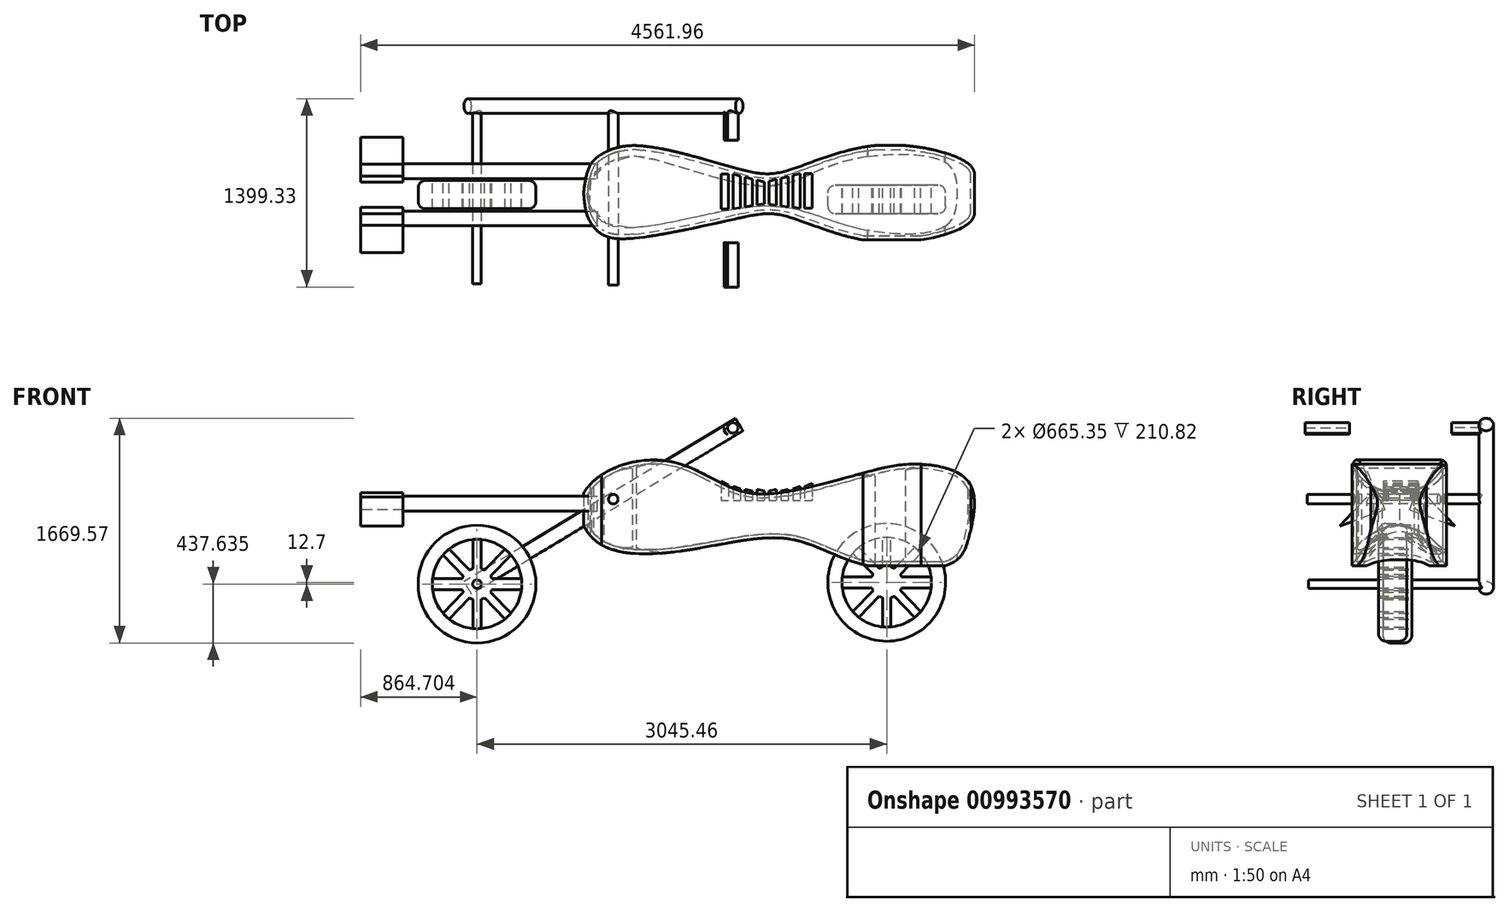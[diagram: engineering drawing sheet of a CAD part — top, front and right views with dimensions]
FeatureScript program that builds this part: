
annotation { "Feature Type Name" : "Feature", "Feature Type Description" : "" }
export const myFeature = defineFeature(function(context is Context, id is Id, definition is map)
    precondition{}
    {
        {
            var Q0;
            Q0=qCreatedBy(makeId("Front.planeOp"),FACE);
            var sketch = newSketch(context, id + "F0", { "sketchPlane" : qUnion([Q0])});
            skFitSpline(sketch, "E0", {"points": [v(-98.98, 13.69) * mm, v(-77.15, 35.34) * mm, v(-39.85, 38.35) * mm, v(-9.17, 24.51) * mm, v(18.5, 19.1) * mm, v(77.75, 32.33) * mm, v(110.84, 37.45) * mm, v(142.12, 25.72) * mm, v(142.12, -6.47) * mm, v(131.6, -23.61) * mm, v(76.55, -24.82) * mm, v(30.53, -8.87) * mm, v(-28.73, -15.19) * mm, v(-86.35, -12.18) * mm, v(-98.98, 13.69) * mm]});
            skSolve(sketch);
        }
        {
            var Q0;
            Q0=makeQuery(id+"F0.imprint","IMPRINT",FACE,{"disambiguationData":[TD([[makeQuery(id+"F0.imprint","IMPRINT",EDGE,{"derivedFrom":sQuery(id+"F0.wireOp",EDGE,"E0")}),-1.0]])]});
            extrude(context, id + "F1", {"entities" : qUnion([Q0]), "depth" : 58.42 * mm, "offsetDistance" : 25.4 * mm});
        }
        {
            var Q0;
            Q0=qCreatedBy(makeId("Top.planeOp"),FACE);
            var sketch = newSketch(context, id + "F2", { "sketchPlane" : qUnion([Q0])});
            skLineSegment(sketch, "E1", {"start": v(-96.89, 0) * mm, "end": v(144, 0) * mm});
            skFitSpline(sketch, "E2", {"points": [v(-96.89, -29.08) * mm, v(-92.88, -12.27) * mm, v(-85.74, -5.4) * mm, v(-64.33, 0) * mm, v(0, -14.66) * mm, v(26.78, -16.16) * mm, v(83.58, 0) * mm, v(143.04, -12.58) * mm, v(145.6, -29.08) * mm], "startDerivative": vector(25.51, 217.38) * mm, "endDerivative": vector(-17.37, -255.32) * mm});
            skFitSpline(sketch, "E3.MirrorCS", {"points": [v(-96.89, -29.08) * mm, v(-93.67, -45.57) * mm, v(-85.74, -54.8) * mm, v(-65.35, -57.37) * mm, v(0, -44.8) * mm, v(26.78, -43.3) * mm, v(83.58, -59.47) * mm, v(143.04, -46.89) * mm, v(145.6, -29.74) * mm], "startDerivative": vector(23.13, -272.3) * mm, "endDerivative": vector(-17.37, 255.32) * mm});
            skFitSpline(sketch, "E4", {"points": [v(-96.89, -29.08) * mm, v(-92.88, -12.27) * mm, v(-85.74, -5.4) * mm, v(-64.33, 0) * mm, v(0, -14.66) * mm, v(26.78, -16.16) * mm, v(83.58, 0) * mm, v(143.04, -12.58) * mm, v(145.6, -29.08) * mm, v(143.04, -46.89) * mm, v(83.58, -59.47) * mm, v(26.78, -43.3) * mm, v(0, -44.8) * mm, v(-65.35, -57.37) * mm, v(-85.74, -54.8) * mm, v(-93.67, -45.57) * mm, v(-96.89, -29.08) * mm]});
            skSolve(sketch);
        }
        {
            var Q0;
            {var subQ4=sQuery(id+"F2.wireOp",EDGE,"E3.MirrorCS");Q0=makeQuery(id+"F2.imprint","IMPRINT",FACE,{"disambiguationData":[TD([[makeQuery(id+"F2.imprint","IMPRINT",EDGE,{"derivedFrom":subQ4}),1.0]])]});}
            extrude(context, id + "F3", {"entities" : qUnion([Q0]), "operationType" : NewBodyOperationType.INTERSECT, "depth" : 68.58 * mm, "offsetDistance" : 25.4 * mm, "hasSecondDirection" : true, "secondDirectionOppositeDirection" : true, "secondDirectionDepth" : 25.4 * mm});
        }
        {
            var Q0;
            {var subQ0=sQuery(id+"F0.wireOp",EDGE,"E0");var subQ1=sQuery(id+"F2.wireOp",EDGE,"E4");var subQ2=sQuery(id+"F2.wireOp",EDGE,"E3.MirrorCS");var subQ3=makeQuery(id+"F2.imprint","INTERSECT",VERTEX,{"disambiguationData":[OD(8.0)],"derivedFrom":[subQ2,subQ1]});Q0=makeQuery(id+"F3.boolean.opBoolean","SPLIT",EDGE,{"disambiguationData":[TD([makeQuery(id+"F3.boolean.toolComplement.opBoolean","COPY",FACE,{"derivedFrom":makeQuery(id+"F3.opExtrude","SWEPT_FACE",FACE,{"disambiguationData":[OSD([subQ2]),TDD([makeQuery(id+"F2.imprint","IMPRINT",EDGE,{"disambiguationData":[TD([[subQ3,-1.0]])],"derivedFrom":subQ2})])]})})])],"derivedFrom":makeQuery(id+"F1.opExtrude","CAP_EDGE",EDGE,{"disambiguationData":[OSD([subQ0])],"isStart":false})});}
            var Q1;
            {var subQ0=sQuery(id+"F2.wireOp",EDGE,"E4");var subQ1=sQuery(id+"F2.wireOp",EDGE,"E3.MirrorCS");Q1=makeQuery(id+"F3.boolean.opBoolean","INTERSECT",EDGE,{"disambiguationData":[OD(1.0)],"derivedFrom":[makeQuery(id+"F1.opExtrude","SWEPT_FACE",FACE,{"disambiguationData":[OSD([sQuery(id+"F0.wireOp",EDGE,"E0")])]}),makeQuery(id+"F3.boolean.toolComplement.opBoolean","COPY",FACE,{"derivedFrom":makeQuery(id+"F3.opExtrude","SWEPT_FACE",FACE,{"disambiguationData":[OSD([subQ1]),TDD([makeQuery(id+"F2.imprint","IMPRINT",EDGE,{"disambiguationData":[TD([[makeQuery(id+"F2.imprint","INTERSECT",VERTEX,{"disambiguationData":[OD(8.0)],"derivedFrom":[subQ1,subQ0]}),-1.0]])],"derivedFrom":subQ1})])]})})]});}
            var Q2;
            {var subQ0=sQuery(id+"F2.wireOp",EDGE,"E4");var subQ1=sQuery(id+"F2.wireOp",EDGE,"E3.MirrorCS");Q2=makeQuery(id+"F3.boolean.opBoolean","INTERSECT",EDGE,{"disambiguationData":[OD(0.0)],"derivedFrom":[makeQuery(id+"F1.opExtrude","SWEPT_FACE",FACE,{"disambiguationData":[OSD([sQuery(id+"F0.wireOp",EDGE,"E0")])]}),makeQuery(id+"F3.boolean.toolComplement.opBoolean","COPY",FACE,{"derivedFrom":makeQuery(id+"F3.opExtrude","SWEPT_FACE",FACE,{"disambiguationData":[OSD([subQ1]),TDD([makeQuery(id+"F2.imprint","IMPRINT",EDGE,{"disambiguationData":[TD([[makeQuery(id+"F2.imprint","INTERSECT",VERTEX,{"disambiguationData":[OD(8.0)],"derivedFrom":[subQ1,subQ0]}),-1.0]])],"derivedFrom":subQ1})])]})})]});}
            var Q3;
            {var subQ0=sQuery(id+"F2.wireOp",EDGE,"E4");var subQ1=sQuery(id+"F2.wireOp",EDGE,"E3.MirrorCS");Q3=makeQuery(id+"F3.boolean.opBoolean","COPY",EDGE,{"derivedFrom":makeQuery(id+"F3.boolean.toolComplement.opBoolean","COPY",EDGE,{"derivedFrom":makeQuery(id+"F3.opExtrude","SWEPT_EDGE",EDGE,{"disambiguationData":[OSD([subQ1,subQ0]),TDD([makeQuery(id+"F2.imprint","INTERSECT",VERTEX,{"disambiguationData":[OD(9.0)],"derivedFrom":[subQ1,subQ0]})])]})})});}
            var Q4;
            Q4=makeQuery(id+"F3.boolean.opBoolean","INTERSECT",EDGE,{"derivedFrom":[makeQuery(id+"F1.opExtrude","CAP_FACE",FACE,{"disambiguationData":[OSD([sQuery(id+"F0.wireOp",EDGE,"E0")])],"isStart":false}),makeQuery(id+"F3.boolean.toolComplement.opBoolean","COPY",FACE,{"derivedFrom":makeQuery(id+"F3.opExtrude","CAP_FACE",FACE,{"disambiguationData":[OSD([sQuery(id+"F2.wireOp",EDGE,"E1"),sQuery(id+"F2.wireOp",EDGE,"E2"),sQuery(id+"F2.wireOp",EDGE,"E3.MirrorCS"),sQuery(id+"F2.wireOp",EDGE,"E4")])],"isStart":true})})]});
            var Q5;
            {var subQ0=sQuery(id+"F2.wireOp",EDGE,"E4");var subQ1=sQuery(id+"F2.wireOp",EDGE,"E3.MirrorCS");Q5=makeQuery(id+"F3.boolean.opBoolean","COPY",EDGE,{"derivedFrom":makeQuery(id+"F3.boolean.toolComplement.opBoolean","COPY",EDGE,{"derivedFrom":makeQuery(id+"F3.opExtrude","CAP_EDGE",EDGE,{"disambiguationData":[OSD([subQ1]),TDD([makeQuery(id+"F2.imprint","IMPRINT",EDGE,{"disambiguationData":[TD([[makeQuery(id+"F2.imprint","INTERSECT",VERTEX,{"disambiguationData":[OD(8.0)],"derivedFrom":[subQ1,subQ0]}),-1.0]])],"derivedFrom":subQ1})])],"isStart":true})})});}
            var Q6;
            {var subQ0=sQuery(id+"F2.wireOp",EDGE,"E4");var subQ1=sQuery(id+"F2.wireOp",EDGE,"E3.MirrorCS");Q6=makeQuery(id+"F3.boolean.opBoolean","INTERSECT",EDGE,{"disambiguationData":[OD(0.0)],"derivedFrom":[makeQuery(id+"F1.opExtrude","SWEPT_FACE",FACE,{"disambiguationData":[OSD([sQuery(id+"F0.wireOp",EDGE,"E0")])]}),makeQuery(id+"F3.boolean.toolComplement.opBoolean","COPY",FACE,{"derivedFrom":makeQuery(id+"F3.opExtrude","SWEPT_FACE",FACE,{"disambiguationData":[OSD([subQ0]),TDD([makeQuery(id+"F2.imprint","IMPRINT",EDGE,{"disambiguationData":[TD([[makeQuery(id+"F2.imprint","INTERSECT",VERTEX,{"disambiguationData":[OD(7.0)],"derivedFrom":[subQ1,subQ0]}),1.0]])],"derivedFrom":subQ0})])]})})]});}
            var Q7;
            {var subQ0=sQuery(id+"F2.wireOp",EDGE,"E4");var subQ1=sQuery(id+"F2.wireOp",EDGE,"E3.MirrorCS");Q7=makeQuery(id+"F3.boolean.opBoolean","INTERSECT",EDGE,{"disambiguationData":[OD(0.0)],"derivedFrom":[makeQuery(id+"F1.opExtrude","SWEPT_FACE",FACE,{"disambiguationData":[OSD([sQuery(id+"F0.wireOp",EDGE,"E0")])]}),makeQuery(id+"F3.boolean.toolComplement.opBoolean","COPY",FACE,{"derivedFrom":makeQuery(id+"F3.opExtrude","SWEPT_FACE",FACE,{"disambiguationData":[OSD([subQ1]),TDD([makeQuery(id+"F2.imprint","IMPRINT",EDGE,{"disambiguationData":[TD([[makeQuery(id+"F2.imprint","INTERSECT",VERTEX,{"disambiguationData":[OD(1.0)],"derivedFrom":[subQ1,subQ0]}),-1.0]])],"derivedFrom":subQ1})])]})})]});}
            var Q8;
            {var subQ0=sQuery(id+"F2.wireOp",EDGE,"E4");var subQ1=sQuery(id+"F2.wireOp",EDGE,"E3.MirrorCS");Q8=makeQuery(id+"F3.boolean.opBoolean","INTERSECT",EDGE,{"disambiguationData":[OD(0.0)],"derivedFrom":[makeQuery(id+"F1.opExtrude","SWEPT_FACE",FACE,{"disambiguationData":[OSD([sQuery(id+"F0.wireOp",EDGE,"E0")])]}),makeQuery(id+"F3.boolean.toolComplement.opBoolean","COPY",FACE,{"derivedFrom":makeQuery(id+"F3.opExtrude","SWEPT_FACE",FACE,{"disambiguationData":[OSD([subQ1]),TDD([makeQuery(id+"F2.imprint","IMPRINT",EDGE,{"disambiguationData":[TD([[makeQuery(id+"F2.imprint","INTERSECT",VERTEX,{"disambiguationData":[OD(0.0)],"derivedFrom":[subQ1,subQ0]}),1.0]])],"derivedFrom":subQ1})])]})})]});}
            var Q9;
            {var subQ0=sQuery(id+"F2.wireOp",EDGE,"E4");var subQ1=sQuery(id+"F2.wireOp",EDGE,"E3.MirrorCS");Q9=makeQuery(id+"F3.boolean.opBoolean","INTERSECT",EDGE,{"disambiguationData":[OD(0.0)],"derivedFrom":[makeQuery(id+"F1.opExtrude","SWEPT_FACE",FACE,{"disambiguationData":[OSD([sQuery(id+"F0.wireOp",EDGE,"E0")])]}),makeQuery(id+"F3.boolean.toolComplement.opBoolean","COPY",FACE,{"derivedFrom":makeQuery(id+"F3.opExtrude","SWEPT_FACE",FACE,{"disambiguationData":[OSD([subQ0]),TDD([makeQuery(id+"F2.imprint","IMPRINT",EDGE,{"disambiguationData":[TD([[makeQuery(id+"F2.imprint","INTERSECT",VERTEX,{"disambiguationData":[OD(5.0)],"derivedFrom":[subQ1,subQ0]}),1.0]])],"derivedFrom":subQ0})])]})})]});}
            var Q10;
            {var subQ0=sQuery(id+"F2.wireOp",EDGE,"E4");var subQ1=sQuery(id+"F2.wireOp",EDGE,"E3.MirrorCS");Q10=makeQuery(id+"F3.boolean.opBoolean","COPY",EDGE,{"derivedFrom":makeQuery(id+"F3.boolean.toolComplement.opBoolean","COPY",EDGE,{"derivedFrom":makeQuery(id+"F3.opExtrude","SWEPT_EDGE",EDGE,{"disambiguationData":[OSD([subQ1,subQ0]),TDD([makeQuery(id+"F2.imprint","INTERSECT",VERTEX,{"disambiguationData":[OD(4.0)],"derivedFrom":[subQ1,subQ0]})])]})})});}
            var Q11;
            {var subQ0=sQuery(id+"F2.wireOp",EDGE,"E4");var subQ1=sQuery(id+"F2.wireOp",EDGE,"E3.MirrorCS");Q11=makeQuery(id+"F3.boolean.opBoolean","INTERSECT",EDGE,{"disambiguationData":[OD(0.0)],"derivedFrom":[makeQuery(id+"F1.opExtrude","SWEPT_FACE",FACE,{"disambiguationData":[OSD([sQuery(id+"F0.wireOp",EDGE,"E0")])]}),makeQuery(id+"F3.boolean.toolComplement.opBoolean","COPY",FACE,{"derivedFrom":makeQuery(id+"F3.opExtrude","SWEPT_FACE",FACE,{"disambiguationData":[OSD([subQ1]),TDD([makeQuery(id+"F2.imprint","IMPRINT",EDGE,{"disambiguationData":[TD([[makeQuery(id+"F2.imprint","INTERSECT",VERTEX,{"disambiguationData":[OD(4.0)],"derivedFrom":[subQ1,subQ0]}),-1.0]])],"derivedFrom":subQ1})])]})})]});}
            var Q12;
            {var subQ0=sQuery(id+"F2.wireOp",EDGE,"E4");var subQ1=sQuery(id+"F2.wireOp",EDGE,"E3.MirrorCS");Q12=makeQuery(id+"F3.boolean.opBoolean","INTERSECT",EDGE,{"disambiguationData":[OD(1.0)],"derivedFrom":[makeQuery(id+"F1.opExtrude","SWEPT_FACE",FACE,{"disambiguationData":[OSD([sQuery(id+"F0.wireOp",EDGE,"E0")])]}),makeQuery(id+"F3.boolean.toolComplement.opBoolean","COPY",FACE,{"derivedFrom":makeQuery(id+"F3.opExtrude","SWEPT_FACE",FACE,{"disambiguationData":[OSD([subQ0]),TDD([makeQuery(id+"F2.imprint","IMPRINT",EDGE,{"disambiguationData":[TD([[makeQuery(id+"F2.imprint","INTERSECT",VERTEX,{"disambiguationData":[OD(5.0)],"derivedFrom":[subQ1,subQ0]}),1.0]])],"derivedFrom":subQ0})])]})})]});}
            var Q13;
            {var subQ0=sQuery(id+"F2.wireOp",EDGE,"E4");var subQ1=sQuery(id+"F2.wireOp",EDGE,"E3.MirrorCS");Q13=makeQuery(id+"F3.boolean.opBoolean","INTERSECT",EDGE,{"disambiguationData":[OD(1.0)],"derivedFrom":[makeQuery(id+"F1.opExtrude","SWEPT_FACE",FACE,{"disambiguationData":[OSD([sQuery(id+"F0.wireOp",EDGE,"E0")])]}),makeQuery(id+"F3.boolean.toolComplement.opBoolean","COPY",FACE,{"derivedFrom":makeQuery(id+"F3.opExtrude","SWEPT_FACE",FACE,{"disambiguationData":[OSD([subQ1]),TDD([makeQuery(id+"F2.imprint","IMPRINT",EDGE,{"disambiguationData":[TD([[makeQuery(id+"F2.imprint","INTERSECT",VERTEX,{"disambiguationData":[OD(4.0)],"derivedFrom":[subQ1,subQ0]}),-1.0]])],"derivedFrom":subQ1})])]})})]});}
            var Q14;
            {var subQ0=sQuery(id+"F2.wireOp",EDGE,"E4");var subQ1=sQuery(id+"F2.wireOp",EDGE,"E3.MirrorCS");Q14=makeQuery(id+"F3.boolean.opBoolean","INTERSECT",EDGE,{"disambiguationData":[OD(1.0)],"derivedFrom":[makeQuery(id+"F1.opExtrude","SWEPT_FACE",FACE,{"disambiguationData":[OSD([sQuery(id+"F0.wireOp",EDGE,"E0")])]}),makeQuery(id+"F3.boolean.toolComplement.opBoolean","COPY",FACE,{"derivedFrom":makeQuery(id+"F3.opExtrude","SWEPT_FACE",FACE,{"disambiguationData":[OSD([subQ1]),TDD([makeQuery(id+"F2.imprint","IMPRINT",EDGE,{"disambiguationData":[TD([[makeQuery(id+"F2.imprint","INTERSECT",VERTEX,{"disambiguationData":[OD(0.0)],"derivedFrom":[subQ1,subQ0]}),1.0]])],"derivedFrom":subQ1})])]})})]});}
            var Q15;
            {var subQ0=sQuery(id+"F2.wireOp",EDGE,"E4");var subQ1=sQuery(id+"F2.wireOp",EDGE,"E3.MirrorCS");Q15=makeQuery(id+"F3.boolean.opBoolean","INTERSECT",EDGE,{"disambiguationData":[OD(1.0)],"derivedFrom":[makeQuery(id+"F1.opExtrude","SWEPT_FACE",FACE,{"disambiguationData":[OSD([sQuery(id+"F0.wireOp",EDGE,"E0")])]}),makeQuery(id+"F3.boolean.toolComplement.opBoolean","COPY",FACE,{"derivedFrom":makeQuery(id+"F3.opExtrude","SWEPT_FACE",FACE,{"disambiguationData":[OSD([subQ1]),TDD([makeQuery(id+"F2.imprint","IMPRINT",EDGE,{"disambiguationData":[TD([[makeQuery(id+"F2.imprint","INTERSECT",VERTEX,{"disambiguationData":[OD(1.0)],"derivedFrom":[subQ1,subQ0]}),-1.0]])],"derivedFrom":subQ1})])]})})]});}
            var Q16;
            {var subQ0=sQuery(id+"F2.wireOp",EDGE,"E4");var subQ1=sQuery(id+"F2.wireOp",EDGE,"E3.MirrorCS");Q16=makeQuery(id+"F3.boolean.opBoolean","INTERSECT",EDGE,{"disambiguationData":[OD(1.0)],"derivedFrom":[makeQuery(id+"F1.opExtrude","SWEPT_FACE",FACE,{"disambiguationData":[OSD([sQuery(id+"F0.wireOp",EDGE,"E0")])]}),makeQuery(id+"F3.boolean.toolComplement.opBoolean","COPY",FACE,{"derivedFrom":makeQuery(id+"F3.opExtrude","SWEPT_FACE",FACE,{"disambiguationData":[OSD([subQ0]),TDD([makeQuery(id+"F2.imprint","IMPRINT",EDGE,{"disambiguationData":[TD([[makeQuery(id+"F2.imprint","INTERSECT",VERTEX,{"disambiguationData":[OD(7.0)],"derivedFrom":[subQ1,subQ0]}),1.0]])],"derivedFrom":subQ0})])]})})]});}
            var Q17;
            {var subQ0=sQuery(id+"F2.wireOp",EDGE,"E4");var subQ1=sQuery(id+"F2.wireOp",EDGE,"E2");Q17=makeQuery(id+"F3.boolean.opBoolean","INTERSECT",EDGE,{"disambiguationData":[OD(1.0)],"derivedFrom":[makeQuery(id+"F1.opExtrude","SWEPT_FACE",FACE,{"disambiguationData":[OSD([sQuery(id+"F0.wireOp",EDGE,"E0")])]}),makeQuery(id+"F3.boolean.toolComplement.opBoolean","COPY",FACE,{"derivedFrom":makeQuery(id+"F3.opExtrude","SWEPT_FACE",FACE,{"disambiguationData":[OSD([subQ1]),TDD([makeQuery(id+"F2.imprint","IMPRINT",EDGE,{"disambiguationData":[TD([[makeQuery(id+"F2.imprint","INTERSECT",VERTEX,{"disambiguationData":[OD(5.0)],"derivedFrom":[subQ1,subQ0]}),1.0]])],"derivedFrom":subQ1})])]})})]});}
            var Q18;
            {var subQ0=sQuery(id+"F2.wireOp",EDGE,"E4");var subQ1=sQuery(id+"F2.wireOp",EDGE,"E2");Q18=makeQuery(id+"F3.boolean.opBoolean","INTERSECT",EDGE,{"disambiguationData":[OD(1.0)],"derivedFrom":[makeQuery(id+"F1.opExtrude","SWEPT_FACE",FACE,{"disambiguationData":[OSD([sQuery(id+"F0.wireOp",EDGE,"E0")])]}),makeQuery(id+"F3.boolean.toolComplement.opBoolean","COPY",FACE,{"derivedFrom":makeQuery(id+"F3.opExtrude","SWEPT_FACE",FACE,{"disambiguationData":[OSD([subQ0]),TDD([makeQuery(id+"F2.imprint","IMPRINT",EDGE,{"disambiguationData":[TD([[makeQuery(id+"F2.imprint","INTERSECT",VERTEX,{"disambiguationData":[OD(5.0)],"derivedFrom":[subQ1,subQ0]}),-1.0]])],"derivedFrom":subQ0})])]})})]});}
            var Q19;
            {var subQ0=sQuery(id+"F2.wireOp",EDGE,"E4");var subQ1=sQuery(id+"F2.wireOp",EDGE,"E2");Q19=makeQuery(id+"F3.boolean.opBoolean","INTERSECT",EDGE,{"disambiguationData":[OD(1.0)],"derivedFrom":[makeQuery(id+"F1.opExtrude","SWEPT_FACE",FACE,{"disambiguationData":[OSD([sQuery(id+"F0.wireOp",EDGE,"E0")])]}),makeQuery(id+"F3.boolean.toolComplement.opBoolean","COPY",FACE,{"derivedFrom":makeQuery(id+"F3.opExtrude","SWEPT_FACE",FACE,{"disambiguationData":[OSD([subQ1]),TDD([makeQuery(id+"F2.imprint","IMPRINT",EDGE,{"disambiguationData":[TD([[makeQuery(id+"F2.imprint","INTERSECT",VERTEX,{"disambiguationData":[OD(6.0)],"derivedFrom":[subQ1,subQ0]}),-1.0]])],"derivedFrom":subQ1})])]})})]});}
            var Q20;
            {var subQ0=sQuery(id+"F2.wireOp",EDGE,"E4");var subQ1=sQuery(id+"F2.wireOp",EDGE,"E2");Q20=makeQuery(id+"F3.boolean.opBoolean","INTERSECT",EDGE,{"disambiguationData":[OD(1.0)],"derivedFrom":[makeQuery(id+"F1.opExtrude","SWEPT_FACE",FACE,{"disambiguationData":[OSD([sQuery(id+"F0.wireOp",EDGE,"E0")])]}),makeQuery(id+"F3.boolean.toolComplement.opBoolean","COPY",FACE,{"derivedFrom":makeQuery(id+"F3.opExtrude","SWEPT_FACE",FACE,{"disambiguationData":[OSD([subQ0]),TDD([makeQuery(id+"F2.imprint","IMPRINT",EDGE,{"disambiguationData":[TD([[makeQuery(id+"F2.imprint","INTERSECT",VERTEX,{"disambiguationData":[OD(7.0)],"derivedFrom":[subQ1,subQ0]}),-1.0]])],"derivedFrom":subQ0})])]})})]});}
            var Q21;
            {var subQ0=sQuery(id+"F0.wireOp",EDGE,"E0");var subQ1=sQuery(id+"F2.wireOp",EDGE,"E4");var subQ2=sQuery(id+"F2.wireOp",EDGE,"E2");Q21=makeQuery(id+"F3.boolean.opBoolean","SPLIT",EDGE,{"disambiguationData":[TD([makeQuery(id+"F1.opExtrude","SWEPT_FACE",FACE,{"disambiguationData":[OSD([subQ0])]}),makeQuery(id+"F1.opExtrude","CAP_FACE",FACE,{"disambiguationData":[OSD([subQ0])],"isStart":true}),makeQuery(id+"F3.boolean.toolComplement.opBoolean","COPY",FACE,{"derivedFrom":makeQuery(id+"F3.opExtrude","SWEPT_FACE",FACE,{"disambiguationData":[OSD([subQ2]),TDD([makeQuery(id+"F2.imprint","IMPRINT",EDGE,{"disambiguationData":[TD([[makeQuery(id+"F2.imprint","INTERSECT",VERTEX,{"disambiguationData":[OD(4.0)],"derivedFrom":[subQ2,subQ1]}),1.0]])],"derivedFrom":subQ2})])]})}),makeQuery(id+"F3.boolean.toolComplement.opBoolean","COPY",FACE,{"derivedFrom":makeQuery(id+"F3.opExtrude","SWEPT_FACE",FACE,{"disambiguationData":[OSD([subQ1]),TDD([makeQuery(id+"F2.imprint","IMPRINT",EDGE,{"disambiguationData":[TD([[makeQuery(id+"F2.imprint","INTERSECT",VERTEX,{"disambiguationData":[OD(7.0)],"derivedFrom":[subQ2,subQ1]}),-1.0]])],"derivedFrom":subQ1})])]})})])],"derivedFrom":makeQuery(id+"F1.opExtrude","CAP_EDGE",EDGE,{"disambiguationData":[OSD([subQ0])],"isStart":true})});}
            var Q22;
            {var subQ0=sQuery(id+"F2.wireOp",EDGE,"E4");Q22=makeQuery(id+"F3.boolean.opBoolean","INTERSECT",EDGE,{"disambiguationData":[OD(1.0)],"derivedFrom":[makeQuery(id+"F1.opExtrude","SWEPT_FACE",FACE,{"disambiguationData":[OSD([sQuery(id+"F0.wireOp",EDGE,"E0")])]}),makeQuery(id+"F3.boolean.toolComplement.opBoolean","COPY",FACE,{"derivedFrom":makeQuery(id+"F3.opExtrude","SWEPT_FACE",FACE,{"disambiguationData":[OSD([subQ0]),TDD([makeQuery(id+"F2.imprint","IMPRINT",EDGE,{"disambiguationData":[TD([[makeQuery(id+"F2.imprint","INTERSECT",VERTEX,{"disambiguationData":[OD(3.0)],"derivedFrom":[sQuery(id+"F2.wireOp",EDGE,"E2"),subQ0]}),-1.0]])],"derivedFrom":subQ0})])]})})]});}
            var Q23;
            {var subQ0=sQuery(id+"F0.wireOp",EDGE,"E0");var subQ1=sQuery(id+"F2.wireOp",EDGE,"E4");var subQ2=sQuery(id+"F2.wireOp",EDGE,"E2");Q23=makeQuery(id+"F3.boolean.opBoolean","SPLIT",EDGE,{"disambiguationData":[TD([makeQuery(id+"F1.opExtrude","SWEPT_FACE",FACE,{"disambiguationData":[OSD([subQ0])]}),makeQuery(id+"F1.opExtrude","CAP_FACE",FACE,{"disambiguationData":[OSD([subQ0])],"isStart":true}),makeQuery(id+"F3.boolean.toolComplement.opBoolean","COPY",FACE,{"derivedFrom":makeQuery(id+"F3.opExtrude","SWEPT_FACE",FACE,{"disambiguationData":[OSD([subQ2]),TDD([makeQuery(id+"F2.imprint","IMPRINT",EDGE,{"disambiguationData":[TD([[makeQuery(id+"F2.imprint","INTERSECT",VERTEX,{"disambiguationData":[OD(5.0)],"derivedFrom":[subQ2,subQ1]}),1.0]])],"derivedFrom":subQ2})])]})}),makeQuery(id+"F3.boolean.toolComplement.opBoolean","COPY",FACE,{"derivedFrom":makeQuery(id+"F3.opExtrude","SWEPT_FACE",FACE,{"disambiguationData":[OSD([subQ1]),TDD([makeQuery(id+"F2.imprint","IMPRINT",EDGE,{"disambiguationData":[TD([[makeQuery(id+"F2.imprint","INTERSECT",VERTEX,{"disambiguationData":[OD(3.0)],"derivedFrom":[subQ2,subQ1]}),-1.0]])],"derivedFrom":subQ1})])]})})]),OD(1.0)],"derivedFrom":makeQuery(id+"F1.opExtrude","CAP_EDGE",EDGE,{"disambiguationData":[OSD([subQ0])],"isStart":true})});}
            var Q24;
            {var subQ0=sQuery(id+"F2.wireOp",EDGE,"E4");var subQ1=sQuery(id+"F2.wireOp",EDGE,"E2");Q24=makeQuery(id+"F3.boolean.opBoolean","INTERSECT",EDGE,{"disambiguationData":[OD(1.0)],"derivedFrom":[makeQuery(id+"F1.opExtrude","SWEPT_FACE",FACE,{"disambiguationData":[OSD([sQuery(id+"F0.wireOp",EDGE,"E0")])]}),makeQuery(id+"F3.boolean.toolComplement.opBoolean","COPY",FACE,{"derivedFrom":makeQuery(id+"F3.opExtrude","SWEPT_FACE",FACE,{"disambiguationData":[OSD([subQ1]),TDD([makeQuery(id+"F2.imprint","IMPRINT",EDGE,{"disambiguationData":[TD([[makeQuery(id+"F2.imprint","INTERSECT",VERTEX,{"disambiguationData":[OD(2.0)],"derivedFrom":[subQ1,subQ0]}),-1.0]])],"derivedFrom":subQ1})])]})})]});}
            var Q25;
            {var subQ0=sQuery(id+"F2.wireOp",EDGE,"E4");var subQ1=sQuery(id+"F2.wireOp",EDGE,"E2");Q25=makeQuery(id+"F3.boolean.opBoolean","COPY",EDGE,{"derivedFrom":makeQuery(id+"F3.boolean.toolComplement.opBoolean","COPY",EDGE,{"derivedFrom":makeQuery(id+"F3.opExtrude","SWEPT_EDGE",EDGE,{"disambiguationData":[OSD([subQ1,subQ0]),TDD([makeQuery(id+"F2.imprint","INTERSECT",VERTEX,{"disambiguationData":[OD(1.0)],"derivedFrom":[subQ1,subQ0]})])]})})});}
            var Q26;
            {var subQ0=sQuery(id+"F2.wireOp",EDGE,"E4");var subQ1=sQuery(id+"F2.wireOp",EDGE,"E2");Q26=makeQuery(id+"F3.boolean.opBoolean","INTERSECT",EDGE,{"disambiguationData":[OD(0.0)],"derivedFrom":[makeQuery(id+"F1.opExtrude","SWEPT_FACE",FACE,{"disambiguationData":[OSD([sQuery(id+"F0.wireOp",EDGE,"E0")])]}),makeQuery(id+"F3.boolean.toolComplement.opBoolean","COPY",FACE,{"derivedFrom":makeQuery(id+"F3.opExtrude","SWEPT_FACE",FACE,{"disambiguationData":[OSD([subQ1]),TDD([makeQuery(id+"F2.imprint","IMPRINT",EDGE,{"disambiguationData":[TD([[makeQuery(id+"F2.imprint","INTERSECT",VERTEX,{"disambiguationData":[OD(2.0)],"derivedFrom":[subQ1,subQ0]}),-1.0]])],"derivedFrom":subQ1})])]})})]});}
            var Q27;
            {var subQ0=sQuery(id+"F2.wireOp",EDGE,"E4");var subQ1=sQuery(id+"F2.wireOp",EDGE,"E2");Q27=makeQuery(id+"F3.boolean.opBoolean","INTERSECT",EDGE,{"disambiguationData":[OD(0.0)],"derivedFrom":[makeQuery(id+"F1.opExtrude","SWEPT_FACE",FACE,{"disambiguationData":[OSD([sQuery(id+"F0.wireOp",EDGE,"E0")])]}),makeQuery(id+"F3.boolean.toolComplement.opBoolean","COPY",FACE,{"derivedFrom":makeQuery(id+"F3.opExtrude","SWEPT_FACE",FACE,{"disambiguationData":[OSD([subQ1]),TDD([makeQuery(id+"F2.imprint","IMPRINT",EDGE,{"disambiguationData":[TD([[makeQuery(id+"F2.imprint","INTERSECT",VERTEX,{"disambiguationData":[OD(5.0)],"derivedFrom":[subQ1,subQ0]}),1.0]])],"derivedFrom":subQ1})])]})})]});}
            var Q28;
            {var subQ0=sQuery(id+"F2.wireOp",EDGE,"E4");Q28=makeQuery(id+"F3.boolean.opBoolean","INTERSECT",EDGE,{"disambiguationData":[OD(0.0)],"derivedFrom":[makeQuery(id+"F1.opExtrude","SWEPT_FACE",FACE,{"disambiguationData":[OSD([sQuery(id+"F0.wireOp",EDGE,"E0")])]}),makeQuery(id+"F3.boolean.toolComplement.opBoolean","COPY",FACE,{"derivedFrom":makeQuery(id+"F3.opExtrude","SWEPT_FACE",FACE,{"disambiguationData":[OSD([subQ0]),TDD([makeQuery(id+"F2.imprint","IMPRINT",EDGE,{"disambiguationData":[TD([[makeQuery(id+"F2.imprint","INTERSECT",VERTEX,{"disambiguationData":[OD(3.0)],"derivedFrom":[sQuery(id+"F2.wireOp",EDGE,"E2"),subQ0]}),-1.0]])],"derivedFrom":subQ0})])]})})]});}
            var Q29;
            {var subQ0=sQuery(id+"F0.wireOp",EDGE,"E0");var subQ1=sQuery(id+"F2.wireOp",EDGE,"E4");var subQ2=sQuery(id+"F2.wireOp",EDGE,"E2");Q29=makeQuery(id+"F3.boolean.opBoolean","SPLIT",EDGE,{"disambiguationData":[TD([makeQuery(id+"F1.opExtrude","SWEPT_FACE",FACE,{"disambiguationData":[OSD([subQ0])]}),makeQuery(id+"F1.opExtrude","CAP_FACE",FACE,{"disambiguationData":[OSD([subQ0])],"isStart":true}),makeQuery(id+"F3.boolean.toolComplement.opBoolean","COPY",FACE,{"derivedFrom":makeQuery(id+"F3.opExtrude","SWEPT_FACE",FACE,{"disambiguationData":[OSD([subQ2]),TDD([makeQuery(id+"F2.imprint","IMPRINT",EDGE,{"disambiguationData":[TD([[makeQuery(id+"F2.imprint","INTERSECT",VERTEX,{"disambiguationData":[OD(5.0)],"derivedFrom":[subQ2,subQ1]}),1.0]])],"derivedFrom":subQ2})])]})}),makeQuery(id+"F3.boolean.toolComplement.opBoolean","COPY",FACE,{"derivedFrom":makeQuery(id+"F3.opExtrude","SWEPT_FACE",FACE,{"disambiguationData":[OSD([subQ1]),TDD([makeQuery(id+"F2.imprint","IMPRINT",EDGE,{"disambiguationData":[TD([[makeQuery(id+"F2.imprint","INTERSECT",VERTEX,{"disambiguationData":[OD(3.0)],"derivedFrom":[subQ2,subQ1]}),-1.0]])],"derivedFrom":subQ1})])]})})]),OD(0.0)],"derivedFrom":makeQuery(id+"F1.opExtrude","CAP_EDGE",EDGE,{"disambiguationData":[OSD([subQ0])],"isStart":true})});}
            var Q30;
            {var subQ0=sQuery(id+"F2.wireOp",EDGE,"E2");Q30=makeQuery(id+"F3.boolean.opBoolean","INTERSECT",EDGE,{"disambiguationData":[OD(1.0)],"derivedFrom":[makeQuery(id+"F1.opExtrude","SWEPT_FACE",FACE,{"disambiguationData":[OSD([sQuery(id+"F0.wireOp",EDGE,"E0")])]}),makeQuery(id+"F3.boolean.toolComplement.opBoolean","COPY",FACE,{"derivedFrom":makeQuery(id+"F3.opExtrude","SWEPT_FACE",FACE,{"disambiguationData":[OSD([subQ0]),TDD([makeQuery(id+"F2.imprint","IMPRINT",EDGE,{"disambiguationData":[TD([[makeQuery(id+"F2.imprint","INTERSECT",VERTEX,{"disambiguationData":[OD(4.0)],"derivedFrom":[subQ0,sQuery(id+"F2.wireOp",EDGE,"E4")]}),1.0]])],"derivedFrom":subQ0})])]})})]});}
            var Q31;
            {var subQ0=sQuery(id+"F2.wireOp",EDGE,"E4");var subQ1=sQuery(id+"F2.wireOp",EDGE,"E2");Q31=makeQuery(id+"F3.boolean.opBoolean","COPY",EDGE,{"derivedFrom":makeQuery(id+"F3.boolean.toolComplement.opBoolean","COPY",EDGE,{"derivedFrom":makeQuery(id+"F3.opExtrude","SWEPT_EDGE",EDGE,{"disambiguationData":[OSD([subQ1,subQ0]),TDD([makeQuery(id+"F2.imprint","INTERSECT",VERTEX,{"disambiguationData":[OD(4.0)],"derivedFrom":[subQ1,subQ0]})])]})})});}
            var Q32;
            {var subQ0=sQuery(id+"F2.wireOp",EDGE,"E2");Q32=makeQuery(id+"F3.boolean.opBoolean","INTERSECT",EDGE,{"disambiguationData":[OD(0.0)],"derivedFrom":[makeQuery(id+"F1.opExtrude","SWEPT_FACE",FACE,{"disambiguationData":[OSD([sQuery(id+"F0.wireOp",EDGE,"E0")])]}),makeQuery(id+"F3.boolean.toolComplement.opBoolean","COPY",FACE,{"derivedFrom":makeQuery(id+"F3.opExtrude","SWEPT_FACE",FACE,{"disambiguationData":[OSD([subQ0]),TDD([makeQuery(id+"F2.imprint","IMPRINT",EDGE,{"disambiguationData":[TD([[makeQuery(id+"F2.imprint","INTERSECT",VERTEX,{"disambiguationData":[OD(4.0)],"derivedFrom":[subQ0,sQuery(id+"F2.wireOp",EDGE,"E4")]}),1.0]])],"derivedFrom":subQ0})])]})})]});}
            var Q33;
            {var subQ0=sQuery(id+"F2.wireOp",EDGE,"E2");Q33=makeQuery(id+"F3.boolean.opBoolean","COPY",EDGE,{"derivedFrom":makeQuery(id+"F3.boolean.toolComplement.opBoolean","COPY",EDGE,{"derivedFrom":makeQuery(id+"F3.opExtrude","CAP_EDGE",EDGE,{"disambiguationData":[OSD([subQ0]),TDD([makeQuery(id+"F2.imprint","IMPRINT",EDGE,{"disambiguationData":[TD([[makeQuery(id+"F2.imprint","INTERSECT",VERTEX,{"disambiguationData":[OD(4.0)],"derivedFrom":[subQ0,sQuery(id+"F2.wireOp",EDGE,"E4")]}),1.0]])],"derivedFrom":subQ0})])],"isStart":true})})});}
            var Q34;
            {var subQ0=sQuery(id+"F2.wireOp",EDGE,"E2");var subQ1=sQuery(id+"F2.wireOp",EDGE,"E1");Q34=makeQuery(id+"F3.boolean.opBoolean","COPY",EDGE,{"derivedFrom":makeQuery(id+"F3.boolean.toolComplement.opBoolean","COPY",EDGE,{"derivedFrom":makeQuery(id+"F3.opExtrude","CAP_EDGE",EDGE,{"disambiguationData":[OSD([subQ1]),TDD([makeQuery(id+"F2.imprint","IMPRINT",EDGE,{"disambiguationData":[TD([[makeQuery(id+"F2.imprint","INTERSECT",VERTEX,{"disambiguationData":[OD(1.0)],"derivedFrom":[subQ1,subQ0]}),1.0]])],"derivedFrom":subQ1})])],"isStart":true})})});}
            var Q35;
            {var subQ0=sQuery(id+"F2.wireOp",EDGE,"E4");var subQ1=sQuery(id+"F2.wireOp",EDGE,"E2");Q35=makeQuery(id+"F3.boolean.opBoolean","INTERSECT",EDGE,{"disambiguationData":[OD(0.0)],"derivedFrom":[makeQuery(id+"F1.opExtrude","SWEPT_FACE",FACE,{"disambiguationData":[OSD([sQuery(id+"F0.wireOp",EDGE,"E0")])]}),makeQuery(id+"F3.boolean.toolComplement.opBoolean","COPY",FACE,{"derivedFrom":makeQuery(id+"F3.opExtrude","SWEPT_FACE",FACE,{"disambiguationData":[OSD([subQ0]),TDD([makeQuery(id+"F2.imprint","IMPRINT",EDGE,{"disambiguationData":[TD([[makeQuery(id+"F2.imprint","INTERSECT",VERTEX,{"disambiguationData":[OD(7.0)],"derivedFrom":[subQ1,subQ0]}),-1.0]])],"derivedFrom":subQ0})])]})})]});}
            fillet(context, id + "F4", {"entities" : qUnion([Q0, Q1, Q2, Q3, Q4, Q5, Q6, Q7, Q8, Q9, Q10, Q11, Q12, Q13, Q14, Q15, Q16, Q17, Q18, Q19, Q20, Q21, Q22, Q23, Q24, Q25, Q26, Q27, Q28, Q29, Q30, Q31, Q32, Q33, Q34, Q35]), "radius" : 3.72 * mm, "tangentPropagation" : true, "allowEdgeOverflow" : false});
        }
        {
            var Q0;
            Q0=qCreatedBy(makeId("Top.planeOp"),FACE);
            var sketch = newSketch(context, id + "F5", { "sketchPlane" : qUnion([Q0])});
            skLineSegment(sketch, "E5.bottom", {"start": v(-11.72, -17.7) * mm, "end": v(-7.07, -17.7) * mm});
            skLineSegment(sketch, "E5.top", {"start": v(-11.72, -39.16) * mm, "end": v(-7.07, -39.16) * mm});
            skLineSegment(sketch, "E5.left", {"start": v(-11.72, -17.7) * mm, "end": v(-11.72, -39.16) * mm});
            skLineSegment(sketch, "E5.right", {"start": v(-7.07, -17.7) * mm, "end": v(-7.07, -39.16) * mm});
            skLineSegment(sketch, "E6.1.0.0", {"start": v(-4.32, -17.65) * mm, "end": v(-4.32, -39.12) * mm});
            skLineSegment(sketch, "E6.1.0.2", {"start": v(0.33, -18.84) * mm, "end": v(0.33, -38.37) * mm});
            skLineSegment(sketch, "E6.2.0.0", {"start": v(3.08, -19.54) * mm, "end": v(3.08, -37.93) * mm});
            skLineSegment(sketch, "E6.2.0.2", {"start": v(7.73, -20.72) * mm, "end": v(7.73, -37.18) * mm});
            skLineSegment(sketch, "E6.3.0.0", {"start": v(10.48, -21.42) * mm, "end": v(10.48, -36.74) * mm});
            skLineSegment(sketch, "E6.3.0.2", {"start": v(15.13, -22.6) * mm, "end": v(15.13, -36) * mm});
            skLineSegment(sketch, "E6.4.0.0", {"start": v(17.87, -21.97) * mm, "end": v(17.87, -36.35) * mm});
            skLineSegment(sketch, "E6.4.0.2", {"start": v(22.52, -20.88) * mm, "end": v(22.52, -36.96) * mm});
            skLineSegment(sketch, "E6.5.0.0", {"start": v(25.27, -20.24) * mm, "end": v(25.27, -37.32) * mm});
            skLineSegment(sketch, "E6.5.0.2", {"start": v(29.92, -19.16) * mm, "end": v(29.92, -37.93) * mm});
            skLineSegment(sketch, "E6.6.0.0", {"start": v(32.67, -18.52) * mm, "end": v(32.67, -38.29) * mm});
            skLineSegment(sketch, "E6.6.0.2", {"start": v(37.32, -17.43) * mm, "end": v(37.32, -38.9) * mm});
            skLineSegment(sketch, "E6.7.0.0", {"start": v(40.07, -17.39) * mm, "end": v(40.07, -38.85) * mm});
            skLineSegment(sketch, "E6.7.0.1", {"start": v(40.07, -17.39) * mm, "end": v(44.72, -17.39) * mm});
            skLineSegment(sketch, "E6.7.0.2", {"start": v(44.72, -17.39) * mm, "end": v(44.72, -38.85) * mm});
            skLineSegment(sketch, "E6.7.0.3", {"start": v(40.07, -38.85) * mm, "end": v(44.72, -38.85) * mm});
            skLineSegment(sketch, "E6.direction1", {"start": v(-11.72, -39.16) * mm, "end": v(-4.32, -39.12) * mm, "construction": true});
            skLineSegment(sketch, "E7", {"start": v(-4.32, -17.65) * mm, "end": v(0.33, -18.84) * mm});
            skLineSegment(sketch, "E8", {"start": v(17.87, -21.97) * mm, "end": v(22.52, -20.88) * mm});
            skLineSegment(sketch, "E9", {"start": v(-4.32, -39.12) * mm, "end": v(0.33, -38.37) * mm});
            skLineSegment(sketch, "E10", {"start": v(17.87, -36.35) * mm, "end": v(22.52, -36.96) * mm});
            skLineSegment(sketch, "E11.trimOffspring", {"start": v(3.08, -19.54) * mm, "end": v(7.73, -20.72) * mm});
            skLineSegment(sketch, "E12.trimOffspring", {"start": v(10.48, -21.42) * mm, "end": v(15.13, -22.6) * mm});
            skLineSegment(sketch, "E13.trimOffspring", {"start": v(25.27, -20.24) * mm, "end": v(29.92, -19.16) * mm});
            skLineSegment(sketch, "E14.trimOffspring", {"start": v(32.67, -18.52) * mm, "end": v(37.32, -17.43) * mm});
            skLineSegment(sketch, "E15.trimOffspring", {"start": v(32.67, -38.29) * mm, "end": v(37.32, -38.9) * mm});
            skLineSegment(sketch, "E16.trimOffspring", {"start": v(25.27, -37.32) * mm, "end": v(29.92, -37.93) * mm});
            skLineSegment(sketch, "E17.trimOffspring", {"start": v(10.48, -36.74) * mm, "end": v(15.13, -36) * mm});
            skLineSegment(sketch, "E18.trimOffspring", {"start": v(3.08, -37.93) * mm, "end": v(7.73, -37.18) * mm});
            skSolve(sketch);
        }
        {
            var Q0;
            Q0 = qSketchRegion(id + "F5", true);
            extrude(context, id + "F6", {"entities" : qUnion([Q0]), "depth" : 27.18 * mm, "offsetDistance" : 25.4 * mm, "hasSecondDirection" : true, "secondDirectionOppositeDirection" : false, "secondDirectionDepth" : 15 * mm});
        }
        {
            var Q0;
            Q0=makeQuery(id+"F6.opExtrude","CAP_EDGE",EDGE,{"disambiguationData":[OSD([sQuery(id+"F5.wireOp",EDGE,"E5.right")])],"isStart":false});
            chamfer(context, id + "F7", {"entities" : qUnion([Q0]), "chamferType" : ChamferType.TWO_OFFSETS, "width1" : 5.08 * mm, "oppositeDirection" : true, "width2" : 2.54 * mm, "tangentPropagation" : true});
        }
        {
            var Q0;
            Q0=makeQuery(id+"F6.opExtrude","CAP_EDGE",EDGE,{"disambiguationData":[OSD([sQuery(id+"F5.wireOp",EDGE,"E6.1.0.2")])],"isStart":false});
            chamfer(context, id + "F8", {"entities" : qUnion([Q0]), "chamferType" : ChamferType.TWO_OFFSETS, "width1" : 5.08 * mm, "oppositeDirection" : false, "width2" : 15.24 * mm, "tangentPropagation" : true});
        }
        {
            var Q0;
            Q0=makeQuery(id+"F6.opExtrude","CAP_EDGE",EDGE,{"disambiguationData":[OSD([sQuery(id+"F5.wireOp",EDGE,"E6.2.0.2")])],"isStart":false});
            var Q1;
            Q1=makeQuery(id+"F6.opExtrude","CAP_EDGE",EDGE,{"disambiguationData":[OSD([sQuery(id+"F5.wireOp",EDGE,"E6.3.0.2")])],"isStart":false});
            chamfer(context, id + "F9", {"entities" : qUnion([Q0, Q1]), "chamferType" : ChamferType.TWO_OFFSETS, "width1" : 6.35 * mm, "oppositeDirection" : false, "width2" : 30.48 * mm, "tangentPropagation" : true});
        }
        {
            var Q0;
            Q0=makeQuery(id+"F6.opExtrude","CAP_EDGE",EDGE,{"disambiguationData":[OSD([sQuery(id+"F5.wireOp",EDGE,"E6.7.0.0")])],"isStart":false});
            chamfer(context, id + "F10", {"entities" : qUnion([Q0]), "chamferType" : ChamferType.TWO_OFFSETS, "width1" : 7.62 * mm, "oppositeDirection" : false, "width2" : 3.8 * mm, "tangentPropagation" : true});
        }
        {
            var Q0;
            Q0=makeQuery(id+"F6.opExtrude","CAP_EDGE",EDGE,{"disambiguationData":[OSD([sQuery(id+"F5.wireOp",EDGE,"E6.6.0.0")])],"isStart":false});
            chamfer(context, id + "F11", {"entities" : qUnion([Q0]), "chamferType" : ChamferType.TWO_OFFSETS, "width1" : 15.24 * mm, "oppositeDirection" : false, "width2" : 5.08 * mm, "tangentPropagation" : true});
        }
        {
            var Q0;
            Q0=makeQuery(id+"F6.opExtrude","CAP_EDGE",EDGE,{"disambiguationData":[OSD([sQuery(id+"F5.wireOp",EDGE,"E6.5.0.0")])],"isStart":false});
            var Q1;
            Q1=makeQuery(id+"F6.opExtrude","CAP_EDGE",EDGE,{"disambiguationData":[OSD([sQuery(id+"F5.wireOp",EDGE,"E6.4.0.0")])],"isStart":false});
            chamfer(context, id + "F12", {"entities" : qUnion([Q0, Q1]), "chamferType" : ChamferType.TWO_OFFSETS, "width1" : 30.48 * mm, "oppositeDirection" : false, "width2" : 6.35 * mm, "tangentPropagation" : true});
        }
        {
            var Q0;
            {var subQ0=sQuery(id+"F2.wireOp",EDGE,"E4");var subQ1=sQuery(id+"F2.wireOp",EDGE,"E3.MirrorCS");var subQ2=makeQuery(id+"F2.imprint","INTERSECT",VERTEX,{"disambiguationData":[OD(0.0)],"derivedFrom":[subQ1,subQ0]});var subQ4=makeQuery(id+"F2.imprint","INTERSECT",VERTEX,{"disambiguationData":[OD(4.0)],"derivedFrom":[subQ1,subQ0]});var subQ5=makeQuery(id+"F2.imprint","INTERSECT",VERTEX,{"disambiguationData":[OD(5.0)],"derivedFrom":[subQ1,subQ0]});var subQ6=sQuery(id+"F2.wireOp",EDGE,"E2");var subQ8=makeQuery(id+"F2.imprint","INTERSECT",VERTEX,{"disambiguationData":[OD(3.0)],"derivedFrom":[subQ1,subQ0]});var subQ9=makeQuery(id+"F2.imprint","INTERSECT",VERTEX,{"disambiguationData":[OD(6.0)],"derivedFrom":[subQ6,subQ0]});var subQ10=makeQuery(id+"F2.imprint","INTERSECT",VERTEX,{"disambiguationData":[OD(7.0)],"derivedFrom":[subQ6,subQ0]});var subQ11=makeQuery(id+"F2.imprint","INTERSECT",VERTEX,{"disambiguationData":[OD(5.0)],"derivedFrom":[subQ6,subQ0]});var subQ12=sQuery(id+"F2.wireOp",EDGE,"E1");var subQ13=makeQuery(id+"F2.imprint","INTERSECT",VERTEX,{"disambiguationData":[OD(2.0)],"derivedFrom":[subQ6,subQ0]});var subQ14=makeQuery(id+"F2.imprint","INTERSECT",VERTEX,{"disambiguationData":[OD(3.0)],"derivedFrom":[subQ6,subQ0]});var subQ15=sQuery(id+"F0.wireOp",EDGE,"E0");var subQ16=makeQuery(id+"F2.imprint","INTERSECT",VERTEX,{"disambiguationData":[OD(1.0)],"derivedFrom":[subQ6,subQ0]});var subQ17=makeQuery(id+"F2.imprint","INTERSECT",VERTEX,{"disambiguationData":[OD(1.0)],"derivedFrom":[subQ1,subQ0]});var subQ18=makeQuery(id+"F2.imprint","INTERSECT",VERTEX,{"disambiguationData":[OD(7.0)],"derivedFrom":[subQ1,subQ0]});Q0=makeQuery(id+"F3.boolean.opBoolean","SPLIT",FACE,{"disambiguationData":[TD([makeQuery(id+"F1.opExtrude","CAP_FACE",FACE,{"disambiguationData":[OSD([subQ15])],"isStart":true}),makeQuery(id+"F1.opExtrude","CAP_FACE",FACE,{"disambiguationData":[OSD([subQ15])],"isStart":false}),makeQuery(id+"F3.boolean.toolComplement.opBoolean","COPY",FACE,{"derivedFrom":makeQuery(id+"F3.opExtrude","CAP_FACE",FACE,{"disambiguationData":[OSD([subQ12,subQ6,subQ1,subQ0])],"isStart":true})}),makeQuery(id+"F3.boolean.toolComplement.opBoolean","COPY",FACE,{"derivedFrom":makeQuery(id+"F3.opExtrude","SWEPT_FACE",FACE,{"disambiguationData":[OSD([subQ6]),TDD([makeQuery(id+"F2.imprint","IMPRINT",EDGE,{"disambiguationData":[TD([[subQ16,1.0]])],"derivedFrom":subQ6})])]})}),makeQuery(id+"F3.boolean.toolComplement.opBoolean","COPY",FACE,{"derivedFrom":makeQuery(id+"F3.opExtrude","SWEPT_FACE",FACE,{"disambiguationData":[OSD([subQ6]),TDD([makeQuery(id+"F2.imprint","IMPRINT",EDGE,{"disambiguationData":[TD([[subQ13,-1.0]])],"derivedFrom":subQ6})])]})}),makeQuery(id+"F3.boolean.toolComplement.opBoolean","COPY",FACE,{"derivedFrom":makeQuery(id+"F3.opExtrude","SWEPT_FACE",FACE,{"disambiguationData":[OSD([subQ6]),TDD([makeQuery(id+"F2.imprint","IMPRINT",EDGE,{"disambiguationData":[TD([[subQ11,1.0]])],"derivedFrom":subQ6})])]})}),makeQuery(id+"F3.boolean.toolComplement.opBoolean","COPY",FACE,{"derivedFrom":makeQuery(id+"F3.opExtrude","SWEPT_FACE",FACE,{"disambiguationData":[OSD([subQ6]),TDD([makeQuery(id+"F2.imprint","IMPRINT",EDGE,{"disambiguationData":[TD([[subQ9,-1.0]])],"derivedFrom":subQ6})])]})}),makeQuery(id+"F3.boolean.toolComplement.opBoolean","COPY",FACE,{"derivedFrom":makeQuery(id+"F3.opExtrude","SWEPT_FACE",FACE,{"disambiguationData":[OSD([subQ1]),TDD([makeQuery(id+"F2.imprint","IMPRINT",EDGE,{"disambiguationData":[TD([[subQ8,1.0]])],"derivedFrom":subQ1})])]})}),makeQuery(id+"F3.boolean.toolComplement.opBoolean","COPY",FACE,{"derivedFrom":makeQuery(id+"F3.opExtrude","SWEPT_FACE",FACE,{"disambiguationData":[OSD([subQ1]),TDD([makeQuery(id+"F2.imprint","IMPRINT",EDGE,{"disambiguationData":[TD([[subQ4,-1.0]])],"derivedFrom":subQ1})])]})}),makeQuery(id+"F3.boolean.toolComplement.opBoolean","COPY",FACE,{"derivedFrom":makeQuery(id+"F3.opExtrude","SWEPT_FACE",FACE,{"disambiguationData":[OSD([subQ1]),TDD([makeQuery(id+"F2.imprint","IMPRINT",EDGE,{"disambiguationData":[TD([[subQ2,1.0]])],"derivedFrom":subQ1})])]})}),makeQuery(id+"F3.boolean.toolComplement.opBoolean","COPY",FACE,{"derivedFrom":makeQuery(id+"F3.opExtrude","SWEPT_FACE",FACE,{"disambiguationData":[OSD([subQ1]),TDD([makeQuery(id+"F2.imprint","IMPRINT",EDGE,{"disambiguationData":[TD([[subQ17,-1.0]])],"derivedFrom":subQ1})])]})}),makeQuery(id+"F3.boolean.toolComplement.opBoolean","COPY",FACE,{"derivedFrom":makeQuery(id+"F3.opExtrude","SWEPT_FACE",FACE,{"disambiguationData":[OSD([subQ0]),TDD([makeQuery(id+"F2.imprint","IMPRINT",EDGE,{"disambiguationData":[TD([[subQ16,-1.0]])],"derivedFrom":subQ0})])]})}),makeQuery(id+"F3.boolean.toolComplement.opBoolean","COPY",FACE,{"derivedFrom":makeQuery(id+"F3.opExtrude","SWEPT_FACE",FACE,{"disambiguationData":[OSD([subQ0]),TDD([makeQuery(id+"F2.imprint","IMPRINT",EDGE,{"disambiguationData":[TD([[subQ14,-1.0]])],"derivedFrom":subQ0})])]})}),makeQuery(id+"F3.boolean.toolComplement.opBoolean","COPY",FACE,{"derivedFrom":makeQuery(id+"F3.opExtrude","SWEPT_FACE",FACE,{"disambiguationData":[OSD([subQ0]),TDD([makeQuery(id+"F2.imprint","IMPRINT",EDGE,{"disambiguationData":[TD([[subQ11,-1.0]])],"derivedFrom":subQ0})])]})}),makeQuery(id+"F3.boolean.toolComplement.opBoolean","COPY",FACE,{"derivedFrom":makeQuery(id+"F3.opExtrude","SWEPT_FACE",FACE,{"disambiguationData":[OSD([subQ0]),TDD([makeQuery(id+"F2.imprint","IMPRINT",EDGE,{"disambiguationData":[TD([[subQ10,-1.0]])],"derivedFrom":subQ0})])]})}),makeQuery(id+"F3.boolean.toolComplement.opBoolean","COPY",FACE,{"derivedFrom":makeQuery(id+"F3.opExtrude","SWEPT_FACE",FACE,{"disambiguationData":[OSD([subQ0]),TDD([makeQuery(id+"F2.imprint","IMPRINT",EDGE,{"disambiguationData":[TD([[subQ18,1.0]])],"derivedFrom":subQ0})])]})}),makeQuery(id+"F3.boolean.toolComplement.opBoolean","COPY",FACE,{"derivedFrom":makeQuery(id+"F3.opExtrude","SWEPT_FACE",FACE,{"disambiguationData":[OSD([subQ0]),TDD([makeQuery(id+"F2.imprint","IMPRINT",EDGE,{"disambiguationData":[TD([[subQ2,1.0]])],"derivedFrom":subQ0})])]})}),makeQuery(id+"F3.boolean.toolComplement.opBoolean","COPY",FACE,{"derivedFrom":makeQuery(id+"F3.opExtrude","SWEPT_FACE",FACE,{"disambiguationData":[OSD([subQ0]),TDD([makeQuery(id+"F2.imprint","IMPRINT",EDGE,{"disambiguationData":[TD([[subQ5,1.0]])],"derivedFrom":subQ0})])]})}),makeQuery(id+"F3.boolean.toolComplement.opBoolean","COPY",FACE,{"derivedFrom":makeQuery(id+"F3.opExtrude","SWEPT_FACE",FACE,{"disambiguationData":[OSD([subQ0]),TDD([makeQuery(id+"F2.imprint","IMPRINT",EDGE,{"disambiguationData":[TD([[subQ8,1.0]])],"derivedFrom":subQ0})])]})})])],"derivedFrom":makeQuery(id+"F1.opExtrude","SWEPT_FACE",FACE,{"disambiguationData":[OSD([subQ15])]})});}
            var Q1;
            Q1=makeQuery(id+"F1.opExtrude","SWEPT_BODY",BODY,{"disambiguationData":[OSD([sQuery(id+"F0.wireOp",EDGE,"E0")])]});
            shell(context, id + "F13", {"isHollow" : true, "entities" : qUnion([Q0]), "parts" : qUnion([Q1]), "thickness" : 2.54 * mm});
        }
        {
            var Q0;
            Q0=qCreatedBy(makeId("Top.planeOp"),FACE);
            var sketch = newSketch(context, id + "F14", { "sketchPlane" : qUnion([Q0])});
            skFitSpline(sketch, "E19", {"points": [v(16.37, -37.15) * mm, v(-30.25, -44.67) * mm, v(-72.36, -50.68) * mm, v(-89.5, -43.46) * mm, v(-94.62, -27.82) * mm, v(-88.6, -15.5) * mm, v(-73.56, -7.37) * mm, v(-51, -9.17) * mm, v(15.47, -25.42) * mm, v(45.85, -16.7) * mm, v(79.54, -6.77) * mm, v(127.97, -10.98) * mm, v(134.58, -29.03) * mm, v(127.67, -49.48) * mm, v(78.94, -52.49) * mm, v(44.05, -41.96) * mm, v(16.37, -37.15) * mm]});
            skSolve(sketch);
        }
        {
            var Q0;
            Q0 = qSketchRegion(id + "F14", true);
            extrude(context, id + "F15", {"entities" : qUnion([Q0]), "operationType" : NewBodyOperationType.REMOVE, "oppositeDirection" : true, "depth" : 25.4 * mm, "offsetDistance" : 25.4 * mm});
        }
        {
            var Q0;
            Q0=makeQuery(id+"F6.opExtrude","SWEPT_BODY",BODY,{"disambiguationData":[OSD([sQuery(id+"F5.wireOp",EDGE,"E6.3.0.0"),sQuery(id+"F5.wireOp",EDGE,"E6.3.0.2"),sQuery(id+"F5.wireOp",EDGE,"E12.trimOffspring"),sQuery(id+"F5.wireOp",EDGE,"E17.trimOffspring")])]});
            var Q1;
            Q1=makeQuery(id+"F6.opExtrude","SWEPT_BODY",BODY,{"disambiguationData":[OSD([sQuery(id+"F5.wireOp",EDGE,"E6.5.0.0"),sQuery(id+"F5.wireOp",EDGE,"E6.5.0.2"),sQuery(id+"F5.wireOp",EDGE,"E13.trimOffspring"),sQuery(id+"F5.wireOp",EDGE,"E16.trimOffspring")])]});
            var Q2;
            Q2=makeQuery(id+"F6.opExtrude","SWEPT_BODY",BODY,{"disambiguationData":[OSD([sQuery(id+"F5.wireOp",EDGE,"E6.1.0.0"),sQuery(id+"F5.wireOp",EDGE,"E6.1.0.2"),sQuery(id+"F5.wireOp",EDGE,"E7"),sQuery(id+"F5.wireOp",EDGE,"E9")])]});
            var Q3;
            Q3=makeQuery(id+"F6.opExtrude","SWEPT_BODY",BODY,{"disambiguationData":[OSD([sQuery(id+"F5.wireOp",EDGE,"E6.7.0.0"),sQuery(id+"F5.wireOp",EDGE,"E6.7.0.1"),sQuery(id+"F5.wireOp",EDGE,"E6.7.0.2"),sQuery(id+"F5.wireOp",EDGE,"E6.7.0.3")])]});
            var Q4;
            Q4=makeQuery(id+"F6.opExtrude","SWEPT_BODY",BODY,{"disambiguationData":[OSD([sQuery(id+"F5.wireOp",EDGE,"E6.2.0.0"),sQuery(id+"F5.wireOp",EDGE,"E6.2.0.2"),sQuery(id+"F5.wireOp",EDGE,"E11.trimOffspring"),sQuery(id+"F5.wireOp",EDGE,"E18.trimOffspring")])]});
            var Q5;
            Q5=makeQuery(id+"F6.opExtrude","SWEPT_BODY",BODY,{"disambiguationData":[OSD([sQuery(id+"F5.wireOp",EDGE,"E6.4.0.0"),sQuery(id+"F5.wireOp",EDGE,"E6.4.0.2"),sQuery(id+"F5.wireOp",EDGE,"E8"),sQuery(id+"F5.wireOp",EDGE,"E10")])]});
            var Q6;
            Q6=makeQuery(id+"F6.opExtrude","SWEPT_BODY",BODY,{"disambiguationData":[OSD([sQuery(id+"F5.wireOp",EDGE,"E5.bottom"),sQuery(id+"F5.wireOp",EDGE,"E5.top"),sQuery(id+"F5.wireOp",EDGE,"E5.left"),sQuery(id+"F5.wireOp",EDGE,"E5.right")])]});
            var Q7;
            Q7=makeQuery(id+"F6.opExtrude","SWEPT_BODY",BODY,{"disambiguationData":[OSD([sQuery(id+"F5.wireOp",EDGE,"E6.6.0.0"),sQuery(id+"F5.wireOp",EDGE,"E6.6.0.2"),sQuery(id+"F5.wireOp",EDGE,"E14.trimOffspring"),sQuery(id+"F5.wireOp",EDGE,"E15.trimOffspring")])]});
            var Q8;
            Q8=makeQuery(id+"F1.opExtrude","SWEPT_BODY",BODY,{"disambiguationData":[OSD([sQuery(id+"F0.wireOp",EDGE,"E0")])]});
            var Q9;
            Q9=qCreatedBy(makeId("Origin.pointOp"),VERTEX);
            transform(context, id + "F16", {"entities" : qUnion([Q0, Q1, Q2, Q3, Q4, Q5, Q6, Q7, Q8]), "transformType" : TransformType.SCALE_UNIFORMLY, "scale" : 12, "scalePoint" : qUnion([Q9]), "makeCopy" : false});
        }
        {
            var Q0;
            Q0=qCreatedBy(makeId("Right.planeOp"),FACE);
            var sketch = newSketch(context, id + "F17", { "sketchPlane" : qUnion([Q0])});
            skCircle(sketch, "E20", {"center": v(-541.6, 155.38) * mm, "radius": 54.7 * mm});
            skCircle(sketch, "E21.MirrorC", {"center": v(-190.26, 155.38) * mm, "radius": 54.7 * mm});
            skSolve(sketch);
        }
        {
            var Q0;
            Q0 = qSketchRegion(id + "F17", true);
            extrude(context, id + "F18", {"entities" : qUnion([Q0]), "oppositeDirection" : true, "depth" : 2819.4 * mm, "offsetDistance" : 25.4 * mm, "hasSecondDirection" : true, "secondDirectionOppositeDirection" : true, "secondDirectionDepth" : 1059.18 * mm});
        }
        {
            var Q0;
            Q0=makeQuery(id+"F18.opExtrude","CAP_FACE",FACE,{"disambiguationData":[OSD([sQuery(id+"F17.wireOp",EDGE,"E20")])],"isStart":false});
            var sketch = newSketch(context, id + "F19", { "sketchPlane" : qUnion([Q0])});
            skCircle(sketch, "E22", {"center": v(541.6, 155.38) * mm, "radius": 52.6 * mm});
            skLineSegment(sketch, "E23.bottom", {"start": v(459.08, 110.63) * mm, "end": v(794.67, -11.51) * mm});
            skLineSegment(sketch, "E23.top", {"start": v(504.88, 236.48) * mm, "end": v(592.43, 204.61) * mm});
            skLineSegment(sketch, "E23.left", {"start": v(459.08, 110.63) * mm, "end": v(504.88, 236.48) * mm});
            skLineSegment(sketch, "E24", {"start": v(794.67, -11.51) * mm, "end": v(592.43, 204.61) * mm});
            skCircle(sketch, "E25", {"center": v(189.94, 156.92) * mm, "radius": 52.73 * mm});
            skCircle(sketch, "E26.MirrorC", {"center": v(189.94, 155.38) * mm, "radius": 52.6 * mm});
            skLineSegment(sketch, "E27.MirrorCS", {"start": v(227.18, 236.57) * mm, "end": v(139.63, 204.7) * mm});
            skLineSegment(sketch, "E28.MirrorCS", {"start": v(272.98, 110.72) * mm, "end": v(227.18, 236.57) * mm});
            skLineSegment(sketch, "E29.MirrorCS", {"start": v(-62.6, -11.42) * mm, "end": v(139.63, 204.7) * mm});
            skLineSegment(sketch, "E30.MirrorCS", {"start": v(272.98, 110.72) * mm, "end": v(-62.6, -11.42) * mm});
            skSolve(sketch);
        }
        {
            var Q0;
            Q0=makeQuery(id+"F19.imprint","IMPRINT",FACE,{"disambiguationData":[TD([[makeQuery(id+"F19.imprint","IMPRINT",EDGE,{"derivedFrom":sQuery(id+"F19.wireOp",EDGE,"E27.MirrorCS")}),1.0]])]});
            var Q1;
            Q1=makeQuery(id+"F19.imprint","IMPRINT",FACE,{"disambiguationData":[TD([[makeQuery(id+"F19.imprint","IMPRINT",EDGE,{"derivedFrom":sQuery(id+"F19.wireOp",EDGE,"E23.bottom")}),1.0]])]});
            extrude(context, id + "F20", {"entities" : qUnion([Q0, Q1]), "operationType" : NewBodyOperationType.ADD, "oppositeDirection" : true, "depth" : 314.96 * mm, "offsetDistance" : 25.4 * mm});
        }
        {
            var Q0;
            Q0=qCreatedBy(makeId("Front.planeOp"),FACE);
            var sketch = newSketch(context, id + "F21", { "sketchPlane" : qUnion([Q0])});
            skCircle(sketch, "E31", {"center": v(-1954.7, -441.8) * mm, "radius": 437.63 * mm});
            skCircle(sketch, "E32", {"center": v(-1954.7, -441.8) * mm, "radius": 332.67 * mm});
            skArc(sketch, "E33", {"start": v(-1985.06, -328.01) * mm, "mid": v(-1997.98, -332.27) * mm, "end": v(-2010.32, -338) * mm});
            skLineSegment(sketch, "E34", {"start": v(-1985.06, -773.1) * mm, "end": v(-1985.06, -555.6) * mm});
            skLineSegment(sketch, "E35.trimOffspring", {"start": v(-1985.06, -328.01) * mm, "end": v(-1985.06, -110.52) * mm});
            skLineSegment(sketch, "E36", {"start": v(-1624.63, -400.25) * mm, "end": v(-1844.5, -400.25) * mm});
            skLineSegment(sketch, "E37.trimOffspring", {"start": v(-2064.9, -400.25) * mm, "end": v(-2284.76, -400.25) * mm});
            skLineSegment(sketch, "E38.MirrorCS", {"start": v(-1924.34, -328.01) * mm, "end": v(-1924.34, -110.52) * mm});
            skLineSegment(sketch, "E39.MirrorCS", {"start": v(-1924.34, -773.1) * mm, "end": v(-1924.34, -555.6) * mm});
            skLineSegment(sketch, "E40.MirrorCS", {"start": v(-1624.63, -483.36) * mm, "end": v(-1844.5, -483.36) * mm});
            skLineSegment(sketch, "E41.MirrorCS", {"start": v(-2064.9, -483.36) * mm, "end": v(-2284.76, -483.36) * mm});
            skLineSegment(sketch, "E42", {"start": v(-2161.44, -702.43) * mm, "end": v(-2010.32, -545.61) * mm});
            skLineSegment(sketch, "E43.MirrorCS", {"start": v(-2207.5, -658.05) * mm, "end": v(-2056.38, -501.23) * mm});
            skLineSegment(sketch, "E44.MirrorCS", {"start": v(-1747.95, -181.18) * mm, "end": v(-1899.07, -338) * mm});
            skLineSegment(sketch, "E45.MirrorCS", {"start": v(-1701.9, -225.56) * mm, "end": v(-1853.02, -382.38) * mm});
            skLineSegment(sketch, "E46.MirrorCS", {"start": v(-1747.95, -702.43) * mm, "end": v(-1899.07, -545.61) * mm});
            skLineSegment(sketch, "E47.MirrorCS", {"start": v(-1701.9, -658.05) * mm, "end": v(-1853.02, -501.23) * mm});
            skLineSegment(sketch, "E48.MirrorCS", {"start": v(-2161.44, -181.18) * mm, "end": v(-2010.32, -338) * mm});
            skLineSegment(sketch, "E49.MirrorCS", {"start": v(-2207.5, -225.56) * mm, "end": v(-2056.38, -382.38) * mm});
            skArc(sketch, "E50.trimOffspring", {"start": v(-1899.07, -338) * mm, "mid": v(-1911.41, -332.27) * mm, "end": v(-1924.34, -328.01) * mm});
            skArc(sketch, "E51.trimOffspring", {"start": v(-1844.5, -400.25) * mm, "mid": v(-1848.38, -391.13) * mm, "end": v(-1853.02, -382.38) * mm});
            skArc(sketch, "E52.trimOffspring", {"start": v(-1853.02, -501.23) * mm, "mid": v(-1848.38, -492.48) * mm, "end": v(-1844.5, -483.36) * mm});
            skArc(sketch, "E53.trimOffspring", {"start": v(-1924.34, -555.6) * mm, "mid": v(-1911.41, -551.34) * mm, "end": v(-1899.07, -545.61) * mm});
            skArc(sketch, "E54.trimOffspring", {"start": v(-2010.32, -545.61) * mm, "mid": v(-1997.98, -551.34) * mm, "end": v(-1985.06, -555.6) * mm});
            skArc(sketch, "E55.trimOffspring", {"start": v(-2064.9, -483.36) * mm, "mid": v(-2061, -492.48) * mm, "end": v(-2056.38, -501.23) * mm});
            skArc(sketch, "E56.trimOffspring", {"start": v(-2056.38, -382.38) * mm, "mid": v(-2061, -391.13) * mm, "end": v(-2064.9, -400.25) * mm});
            skSolve(sketch);
        }
        {
            var Q0;
            Q0=makeQuery(id+"F21.imprint","IMPRINT",FACE,{"disambiguationData":[TD([[makeQuery(id+"F21.imprint","IMPRINT",EDGE,{"derivedFrom":sQuery(id+"F21.wireOp",EDGE,"E31")}),1.0]])]});
            extrude(context, id + "F22", {"entities" : qUnion([Q0]), "depth" : 457.2 * mm, "offsetDistance" : 25.4 * mm, "hasSecondDirection" : true, "secondDirectionOppositeDirection" : false, "secondDirectionDepth" : 246.38 * mm});
        }
        {
            var Q0;
            Q0=makeQuery(id+"F21.imprint","IMPRINT",FACE,{"disambiguationData":[TD([[makeQuery(id+"F21.imprint","IMPRINT",EDGE,{"derivedFrom":sQuery(id+"F21.wireOp",EDGE,"E33")}),1.0]])]});
            extrude(context, id + "F23", {"entities" : qUnion([Q0]), "depth" : 457.2 * mm, "offsetDistance" : 25.4 * mm, "hasSecondDirection" : true, "secondDirectionOppositeDirection" : false, "secondDirectionDepth" : 246.38 * mm});
        }
        {
            var Q0;
            Q0=makeQuery(id+"F22.opExtrude","CAP_EDGE",EDGE,{"disambiguationData":[OSD([sQuery(id+"F21.wireOp",EDGE,"E31")])],"isStart":false});
            var Q1;
            Q1=makeQuery(id+"F22.opExtrude","CAP_EDGE",EDGE,{"disambiguationData":[OSD([sQuery(id+"F21.wireOp",EDGE,"E31")])],"isStart":true});
            fillet(context, id + "F24", {"entities" : qUnion([Q0, Q1]), "radius" : 55.19 * mm, "tangentPropagation" : true, "allowEdgeOverflow" : false});
        }
        {
            var Q0;
            Q0=makeQuery(id+"F23.opExtrude","SWEPT_BODY",BODY,{"disambiguationData":[OSD([sQuery(id+"F21.wireOp",EDGE,"E32"),sQuery(id+"F21.wireOp",EDGE,"E33"),sQuery(id+"F21.wireOp",EDGE,"E34"),sQuery(id+"F21.wireOp",EDGE,"E35.trimOffspring"),sQuery(id+"F21.wireOp",EDGE,"E36"),sQuery(id+"F21.wireOp",EDGE,"E37.trimOffspring"),sQuery(id+"F21.wireOp",EDGE,"E38.MirrorCS"),sQuery(id+"F21.wireOp",EDGE,"E39.MirrorCS"),sQuery(id+"F21.wireOp",EDGE,"E40.MirrorCS"),sQuery(id+"F21.wireOp",EDGE,"E41.MirrorCS"),sQuery(id+"F21.wireOp",EDGE,"E42"),sQuery(id+"F21.wireOp",EDGE,"E43.MirrorCS"),sQuery(id+"F21.wireOp",EDGE,"E44.MirrorCS"),sQuery(id+"F21.wireOp",EDGE,"E45.MirrorCS"),sQuery(id+"F21.wireOp",EDGE,"E46.MirrorCS"),sQuery(id+"F21.wireOp",EDGE,"E47.MirrorCS"),sQuery(id+"F21.wireOp",EDGE,"E48.MirrorCS"),sQuery(id+"F21.wireOp",EDGE,"E49.MirrorCS"),sQuery(id+"F21.wireOp",EDGE,"E50.trimOffspring"),sQuery(id+"F21.wireOp",EDGE,"E51.trimOffspring"),sQuery(id+"F21.wireOp",EDGE,"E52.trimOffspring"),sQuery(id+"F21.wireOp",EDGE,"E53.trimOffspring"),sQuery(id+"F21.wireOp",EDGE,"E54.trimOffspring"),sQuery(id+"F21.wireOp",EDGE,"E55.trimOffspring"),sQuery(id+"F21.wireOp",EDGE,"E56.trimOffspring")])]});
            var Q1;
            Q1=makeQuery(id+"F22.opExtrude","SWEPT_BODY",BODY,{"disambiguationData":[OSD([sQuery(id+"F21.wireOp",EDGE,"E31"),sQuery(id+"F21.wireOp",EDGE,"E32")])]});
            transform(context, id + "F25", {"entities" : qUnion([Q0, Q1]), "transformType" : TransformType.TRANSLATION_3D, "dx" : 3045.46 * mm, "dy" : -35.56 * mm, "dz" : 12.7 * mm, "makeCopy" : true});
        }
        {
            var Q0;
            Q0=makeQuery(id+"F22.opExtrude","SWEPT_BODY",BODY,{"disambiguationData":[OSD([sQuery(id+"F21.wireOp",EDGE,"E31"),sQuery(id+"F21.wireOp",EDGE,"E32")])]});
            var Q1;
            Q1=makeQuery(id+"F25.opPattern","COPY",BODY,{"derivedFrom":makeQuery(id+"F22.opExtrude","SWEPT_BODY",BODY,{"disambiguationData":[OSD([sQuery(id+"F21.wireOp",EDGE,"E31"),sQuery(id+"F21.wireOp",EDGE,"E32")])]}),"instanceName":"1"});
            var Q2;
            Q2=makeQuery(id+"F23.opExtrude","SWEPT_BODY",BODY,{"disambiguationData":[OSD([sQuery(id+"F21.wireOp",EDGE,"E32"),sQuery(id+"F21.wireOp",EDGE,"E33"),sQuery(id+"F21.wireOp",EDGE,"E34"),sQuery(id+"F21.wireOp",EDGE,"E35.trimOffspring"),sQuery(id+"F21.wireOp",EDGE,"E36"),sQuery(id+"F21.wireOp",EDGE,"E37.trimOffspring"),sQuery(id+"F21.wireOp",EDGE,"E38.MirrorCS"),sQuery(id+"F21.wireOp",EDGE,"E39.MirrorCS"),sQuery(id+"F21.wireOp",EDGE,"E40.MirrorCS"),sQuery(id+"F21.wireOp",EDGE,"E41.MirrorCS"),sQuery(id+"F21.wireOp",EDGE,"E42"),sQuery(id+"F21.wireOp",EDGE,"E43.MirrorCS"),sQuery(id+"F21.wireOp",EDGE,"E44.MirrorCS"),sQuery(id+"F21.wireOp",EDGE,"E45.MirrorCS"),sQuery(id+"F21.wireOp",EDGE,"E46.MirrorCS"),sQuery(id+"F21.wireOp",EDGE,"E47.MirrorCS"),sQuery(id+"F21.wireOp",EDGE,"E48.MirrorCS"),sQuery(id+"F21.wireOp",EDGE,"E49.MirrorCS"),sQuery(id+"F21.wireOp",EDGE,"E50.trimOffspring"),sQuery(id+"F21.wireOp",EDGE,"E51.trimOffspring"),sQuery(id+"F21.wireOp",EDGE,"E52.trimOffspring"),sQuery(id+"F21.wireOp",EDGE,"E53.trimOffspring"),sQuery(id+"F21.wireOp",EDGE,"E54.trimOffspring"),sQuery(id+"F21.wireOp",EDGE,"E55.trimOffspring"),sQuery(id+"F21.wireOp",EDGE,"E56.trimOffspring")])]});
            var Q3;
            Q3=makeQuery(id+"F25.opPattern","COPY",BODY,{"derivedFrom":makeQuery(id+"F23.opExtrude","SWEPT_BODY",BODY,{"disambiguationData":[OSD([sQuery(id+"F21.wireOp",EDGE,"E32"),sQuery(id+"F21.wireOp",EDGE,"E33"),sQuery(id+"F21.wireOp",EDGE,"E34"),sQuery(id+"F21.wireOp",EDGE,"E35.trimOffspring"),sQuery(id+"F21.wireOp",EDGE,"E36"),sQuery(id+"F21.wireOp",EDGE,"E37.trimOffspring"),sQuery(id+"F21.wireOp",EDGE,"E38.MirrorCS"),sQuery(id+"F21.wireOp",EDGE,"E39.MirrorCS"),sQuery(id+"F21.wireOp",EDGE,"E40.MirrorCS"),sQuery(id+"F21.wireOp",EDGE,"E41.MirrorCS"),sQuery(id+"F21.wireOp",EDGE,"E42"),sQuery(id+"F21.wireOp",EDGE,"E43.MirrorCS"),sQuery(id+"F21.wireOp",EDGE,"E44.MirrorCS"),sQuery(id+"F21.wireOp",EDGE,"E45.MirrorCS"),sQuery(id+"F21.wireOp",EDGE,"E46.MirrorCS"),sQuery(id+"F21.wireOp",EDGE,"E47.MirrorCS"),sQuery(id+"F21.wireOp",EDGE,"E48.MirrorCS"),sQuery(id+"F21.wireOp",EDGE,"E49.MirrorCS"),sQuery(id+"F21.wireOp",EDGE,"E50.trimOffspring"),sQuery(id+"F21.wireOp",EDGE,"E51.trimOffspring"),sQuery(id+"F21.wireOp",EDGE,"E52.trimOffspring"),sQuery(id+"F21.wireOp",EDGE,"E53.trimOffspring"),sQuery(id+"F21.wireOp",EDGE,"E54.trimOffspring"),sQuery(id+"F21.wireOp",EDGE,"E55.trimOffspring"),sQuery(id+"F21.wireOp",EDGE,"E56.trimOffspring")])]}),"instanceName":"1"});
            transform(context, id + "F26", {"entities" : qUnion([Q0, Q1, Q2, Q3]), "transformType" : TransformType.TRANSLATION_3D, "dx" : 0 * mm, "dy" : -12.7 * mm, "dz" : 0 * mm, "makeCopy" : false});
        }
        {
            var Q0;
            Q0=makeQuery(id+"F23.opExtrude","SWEPT_FACE",FACE,{"disambiguationData":[OSD([sQuery(id+"F21.wireOp",EDGE,"E47.MirrorCS")])]});
            var sketch = newSketch(context, id + "F27", { "sketchPlane" : qUnion([Q0])});
            skCircle(sketch, "E57", {"center": v(293.72, 1187.95) * mm, "radius": 54.05 * mm});
            skPoint(sketch, "E58.startSnap0", {"position": v(-364.5, 924.9) * mm});
            skCircle(sketch, "E59.MirrorC", {"center": v(-1022.7, 1187.95) * mm, "radius": 54.05 * mm});
            skSolve(sketch);
        }
        {
            var Q0;
            Q0=makeQuery(id+"F27.imprint","IMPRINT",FACE,{"disambiguationData":[TD([[makeQuery(id+"F27.imprint","IMPRINT",EDGE,{"derivedFrom":sQuery(id+"F27.wireOp",EDGE,"E57")}),1.0]])]});
            var Q1;
            Q1=makeQuery(id+"F27.imprint","IMPRINT",FACE,{"disambiguationData":[TD([[makeQuery(id+"F27.imprint","IMPRINT",EDGE,{"derivedFrom":sQuery(id+"F27.wireOp",EDGE,"E59.MirrorC")}),-1.0]])]});
            extrude(context, id + "F28", {"entities" : qUnion([Q0, Q1]), "depth" : 2354.58 * mm, "offsetDistance" : 25.4 * mm});
        }
        {
            var Q0;
            Q0=makeQuery(id+"F28.opExtrude","SWEPT_BODY",BODY,{"disambiguationData":[OSD([sQuery(id+"F27.wireOp",EDGE,"E57")])]});
            var Q1;
            Q1=makeQuery(id+"F28.opExtrude","SWEPT_BODY",BODY,{"disambiguationData":[OSD([sQuery(id+"F27.wireOp",EDGE,"E59.MirrorC")])]});
            transform(context, id + "F29", {"entities" : qUnion([Q0, Q1]), "transformType" : TransformType.TRANSLATION_3D, "dx" : 20.32 * mm, "dy" : 0 * mm, "dz" : -172.72 * mm, "makeCopy" : false});
        }
        {
            var Q0;
            Q0=makeQuery(id+"F28.opExtrude","SWEPT_BODY",BODY,{"disambiguationData":[OSD([sQuery(id+"F27.wireOp",EDGE,"E57")])]});
            var Q1;
            Q1=makeQuery(id+"F28.opExtrude","SWEPT_BODY",BODY,{"disambiguationData":[OSD([sQuery(id+"F27.wireOp",EDGE,"E59.MirrorC")])]});
            var Q2;
            {var subQ0=sQuery(id+"F21.wireOp",EDGE,"E31");Q2=makeQuery(id+"F24.opFillet","BLEND_EDGE",EDGE,{"blendedFrom":[makeQuery(id+"F22.opExtrude","CAP_EDGE",EDGE,{"disambiguationData":[OSD([subQ0])],"isStart":true}),makeQuery(id+"F22.opExtrude","SWEPT_FACE",FACE,{"disambiguationData":[OSD([subQ0])]})],"blendedInto":[makeQuery(id+"F22.opExtrude","SWEPT_FACE",FACE,{"disambiguationData":[OSD([subQ0])]})]});}
            transform(context, id + "F30", {"entities" : qUnion([Q0, Q1]), "transformType" : TransformType.ROTATION, "transformAxis" : qUnion([Q2]), "angle" : 12.9 * degree, "oppositeDirection" : true, "makeCopy" : false});
        }
        {
            var Q0;
            Q0=makeQuery(id+"F23.opExtrude","CAP_FACE",FACE,{"disambiguationData":[OSD([sQuery(id+"F21.wireOp",EDGE,"E32"),sQuery(id+"F21.wireOp",EDGE,"E33"),sQuery(id+"F21.wireOp",EDGE,"E34"),sQuery(id+"F21.wireOp",EDGE,"E35.trimOffspring"),sQuery(id+"F21.wireOp",EDGE,"E36"),sQuery(id+"F21.wireOp",EDGE,"E37.trimOffspring"),sQuery(id+"F21.wireOp",EDGE,"E38.MirrorCS"),sQuery(id+"F21.wireOp",EDGE,"E39.MirrorCS"),sQuery(id+"F21.wireOp",EDGE,"E40.MirrorCS"),sQuery(id+"F21.wireOp",EDGE,"E41.MirrorCS"),sQuery(id+"F21.wireOp",EDGE,"E42"),sQuery(id+"F21.wireOp",EDGE,"E43.MirrorCS"),sQuery(id+"F21.wireOp",EDGE,"E44.MirrorCS"),sQuery(id+"F21.wireOp",EDGE,"E45.MirrorCS"),sQuery(id+"F21.wireOp",EDGE,"E46.MirrorCS"),sQuery(id+"F21.wireOp",EDGE,"E47.MirrorCS"),sQuery(id+"F21.wireOp",EDGE,"E48.MirrorCS"),sQuery(id+"F21.wireOp",EDGE,"E49.MirrorCS"),sQuery(id+"F21.wireOp",EDGE,"E50.trimOffspring"),sQuery(id+"F21.wireOp",EDGE,"E51.trimOffspring"),sQuery(id+"F21.wireOp",EDGE,"E52.trimOffspring"),sQuery(id+"F21.wireOp",EDGE,"E53.trimOffspring"),sQuery(id+"F21.wireOp",EDGE,"E54.trimOffspring"),sQuery(id+"F21.wireOp",EDGE,"E55.trimOffspring"),sQuery(id+"F21.wireOp",EDGE,"E56.trimOffspring")])],"isStart":true});
            var sketch = newSketch(context, id + "F31", { "sketchPlane" : qUnion([Q0])});
            skCircle(sketch, "E60", {"center": v(1954.7, -441.8) * mm, "radius": 31.98 * mm});
            skCircle(sketch, "E61", {"center": v(53.1, 718.62) * mm, "radius": 38.77 * mm});
            skArc(sketch, "E62", {"start": v(92.89, 671.3) * mm, "mid": v(110.53, 691.76) * mm, "end": v(113.32, 718.62) * mm});
            skArc(sketch, "E63", {"start": v(92.89, 671.3) * mm, "mid": v(115.32, 689.69) * mm, "end": v(113.32, 718.62) * mm});
            skCircle(sketch, "E64", {"center": v(941.8, 188.92) * mm, "radius": 35.46 * mm});
            skSolve(sketch);
        }
        {
            var Q0;
            Q0=makeQuery(id+"F31.imprint","IMPRINT",FACE,{"disambiguationData":[TD([[makeQuery(id+"F31.imprint","IMPRINT",EDGE,{"derivedFrom":sQuery(id+"F31.wireOp",EDGE,"E60")}),1.0]])]});
            extrude(context, id + "F32", {"entities" : qUnion([Q0]), "operationType" : NewBodyOperationType.ADD, "depth" : 525.78 * mm, "offsetDistance" : 25.4 * mm, "hasSecondDirection" : true, "secondDirectionOppositeDirection" : true, "secondDirectionDepth" : 767.08 * mm});
        }
        {
            var Q0;
            Q0=makeQuery(id+"F31.imprint","IMPRINT",FACE,{"disambiguationData":[TD([[makeQuery(id+"F31.imprint","IMPRINT",EDGE,{"derivedFrom":sQuery(id+"F31.wireOp",EDGE,"E61")}),1.0]])]});
            var Q1;
            Q1=makeQuery(id+"F31.imprint","IMPRINT",FACE,{"disambiguationData":[TD([[makeQuery(id+"F31.imprint","IMPRINT",EDGE,{"derivedFrom":sQuery(id+"F31.wireOp",EDGE,"E62")}),-1.0]])]});
            extrude(context, id + "F33", {"entities" : qUnion([Q0, Q1]), "operationType" : NewBodyOperationType.ADD, "depth" : 551.18 * mm, "offsetDistance" : 25.4 * mm, "hasSecondDirection" : true, "secondDirectionOppositeDirection" : false, "secondDirectionDepth" : 297.18 * mm});
        }
        {
            var Q0;
            Q0=makeQuery(id+"F31.imprint","IMPRINT",FACE,{"disambiguationData":[TD([[makeQuery(id+"F31.imprint","IMPRINT",EDGE,{"derivedFrom":sQuery(id+"F31.wireOp",EDGE,"E61")}),1.0]])]});
            var Q1;
            Q1=makeQuery(id+"F31.imprint","IMPRINT",FACE,{"disambiguationData":[TD([[makeQuery(id+"F31.imprint","IMPRINT",EDGE,{"derivedFrom":sQuery(id+"F31.wireOp",EDGE,"E62")}),-1.0]])]});
            extrude(context, id + "F34", {"entities" : qUnion([Q0, Q1]), "operationType" : NewBodyOperationType.ADD, "oppositeDirection" : true, "depth" : 792.48 * mm, "offsetDistance" : 25.4 * mm, "hasSecondDirection" : true, "secondDirectionOppositeDirection" : true, "secondDirectionDepth" : 462.28 * mm});
        }
        {
            var Q0;
            Q0=makeQuery(id+"F31.imprint","IMPRINT",FACE,{"disambiguationData":[TD([[makeQuery(id+"F31.imprint","IMPRINT",EDGE,{"derivedFrom":sQuery(id+"F31.wireOp",EDGE,"E64")}),1.0]])]});
            extrude(context, id + "F35", {"entities" : qUnion([Q0]), "operationType" : NewBodyOperationType.ADD, "depth" : 538.48 * mm, "offsetDistance" : 25.4 * mm, "hasSecondDirection" : true, "secondDirectionOppositeDirection" : true, "secondDirectionDepth" : 777.24 * mm});
        }
    });
